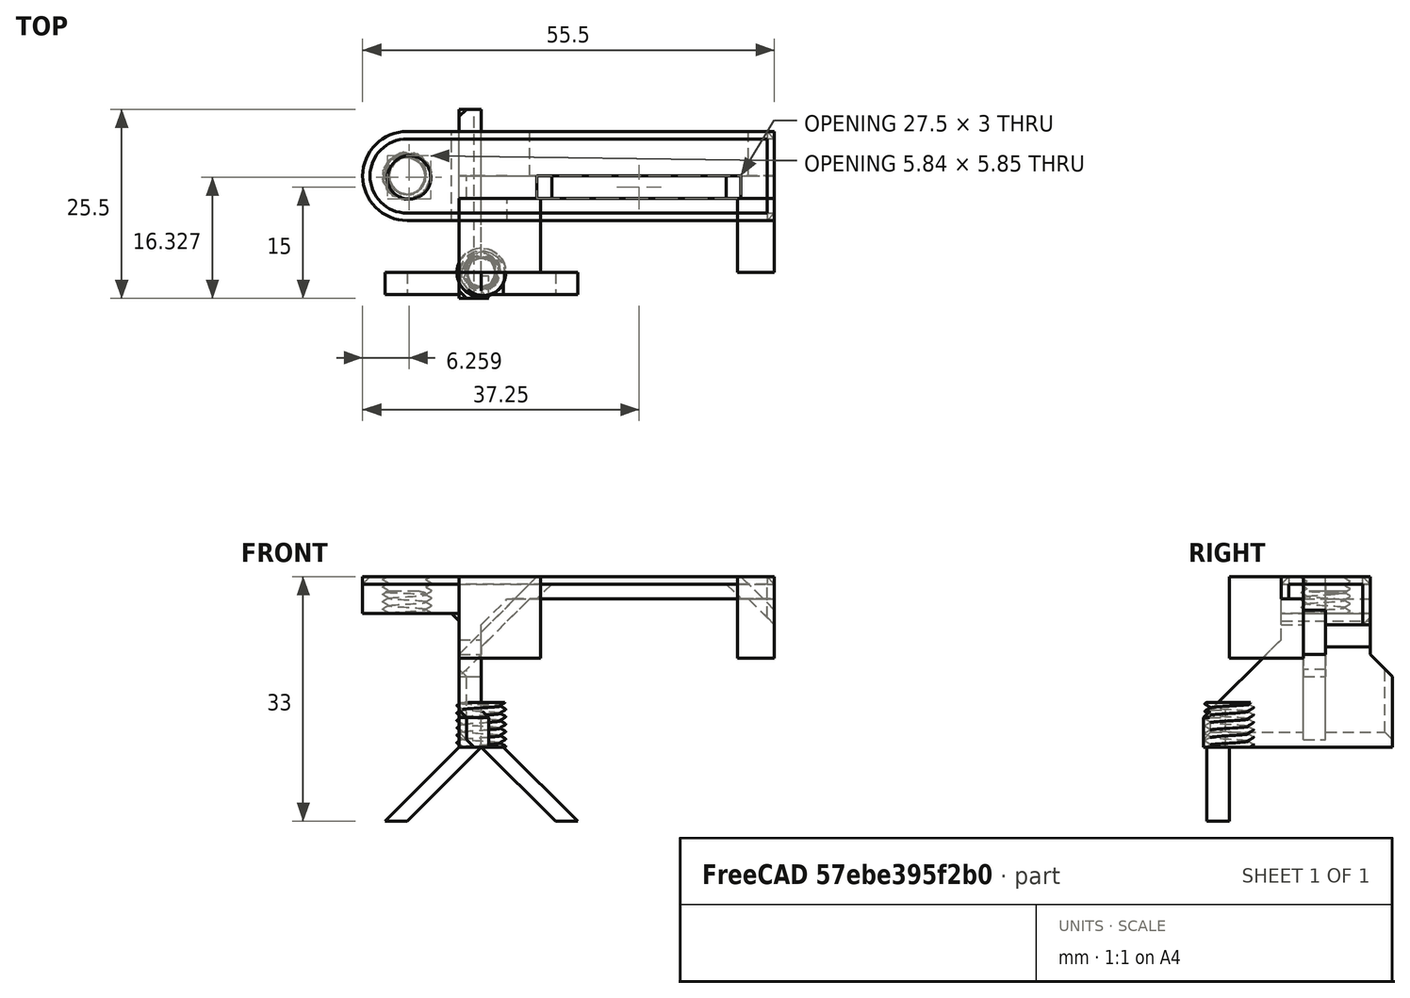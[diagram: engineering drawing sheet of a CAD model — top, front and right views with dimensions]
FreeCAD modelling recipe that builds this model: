
FCSTD DOCUMENT  (FreeCAD 0.18R14555 (Git shallow))
Label: rev-bowden-on-X-fix
License: All rights reserved
LicenseURL: http://en.wikipedia.org/wiki/All_rights_reserved
objects: Part::Box×13, Part::Cut×11, Part::Chamfer×7, Part::Feature×7, Part::MultiFuse×3, Part::Cylinder×2, Sketcher::SketchObject×1, PartDesign::Pad×1, PartDesign::Body×1, Part::Mirroring×1
note: 48 computed .brp shape members not serialized (recipe doc carries the construction recipe); baked Part::Feature solids carry a one-line shape summary decoded from their .brp

FEATURE [Part::Box] Box  label="Cube"
  AttacherType = Attacher::AttachEngine3D
  Height = 20
  Length = 42.5
  Width = 10
FEATURE [Part::Box] Box001  label="Cube001"
  AttacherType = Attacher::AttachEngine3D
  Height = 23
  Length = 42.5
  Placement = pos=(-3,0,0) rot=(0,0,1;0rad)
  Width = 19
FEATURE [Part::Box] Box002  label="Cube002"
  AttacherType = Attacher::AttachEngine3D
  Height = 11
  Length = 11
  Placement = pos=(-3,0,12) rot=(0,0,1;0rad)
  Width = 10
FEATURE [Part::Box] Box003  label="Cube003"
  AttacherType = Attacher::AttachEngine3D
  Height = 11
  Length = 5
  Placement = pos=(34.5,0,12) rot=(0,0,1;0rad)
  Width = 10
FEATURE [Part::Chamfer] Chamfer
  Base = -> Box
  Edges = 2 edges r=3.5: [Edge2,Edge6]
FEATURE [Part::Cylinder] Cylinder
  Angle = 360
  AttacherType = Attacher::AttachEngine3D
  Height = 5
  Placement = pos=(-10,11,18) rot=(0,0,1;0rad)
  Radius = 6
FEATURE [Sketcher::SketchObject] Sketch
  MapMode = 5
  Placement = pos=(0,0,0) rot=(1,0,0;1.5708rad)
  Support = -> [XZ_Plane]
  sketch-geometry (4):
    g0: LineSegment StartX=0 StartY=0 StartZ=0 EndX=10 EndY=-10 EndZ=0
    g1: LineSegment StartX=0 StartY=0 StartZ=0 EndX=3 EndY=0 EndZ=0
    g2: LineSegment StartX=10 StartY=-10 StartZ=0 EndX=13 EndY=-10 EndZ=0
    g3: LineSegment StartX=13 StartY=-10 StartZ=0 EndX=3 EndY=0 EndZ=0
FEATURE [PartDesign::Pad] Pad
  Length = 3
  Length2 = 100
  Placement = pos=(0,0,0) rot=(1,0,0;1.5708rad)
  Profile = -> Sketch
  Type = 0
FEATURE [PartDesign::Body] Body
  Group = -> [Sketch,Pad]
  Origin = -> Origin
  Tip = -> Pad
FEATURE [Part::Feature] Body001
  Placement = pos=(30.5,13,24.5) rot=(0,0,1;0rad)
  shape: bbox 13 x 3 x 10 mm, 6 faces (baked)
FEATURE [Part::Mirroring] Part__Mirroring  label="Pad (Mirror #1)"
  Base = (0,0,0)
  Normal = (1,0,0)
  Source = -> Pad
FEATURE [Part::Feature] Part__Mirroring001  label="Pad (Mirror #1)001"
  Placement = pos=(11.5,13,24) rot=(0,0,1;0rad)
  shape: bbox 13 x 3 x 10 mm, 6 faces (baked)
FEATURE [Part::Feature] Part__Mirroring002  label="Pad (Mirror #1)002"
  Placement = pos=(4.5,13,17) rot=(0,0,1;0rad)
  shape: bbox 13 x 3 x 10 mm, 6 faces (baked)
FEATURE [Part::Box] Box006  label="Cube006"
  AttacherType = Attacher::AttachEngine3D
  Height = 11
  Length = 1
  Placement = pos=(-3,10,0) rot=(0,0,1;0rad)
  Width = 3
FEATURE [Part::Box] Box007  label="Cube007"
  AttacherType = Attacher::AttachEngine3D
  Height = 1
  Length = 24
  Placement = pos=(9,10,22) rot=(0,0,1;0rad)
  Width = 3
FEATURE [Part::Feature] Part__Feature  label="1"
  shape: bbox 11.55 x 19.8 x 11.8 mm, 29 faces (baked)
FEATURE [Part::Cylinder] Cylinder001
  Angle = 360
  AttacherType = Attacher::AttachEngine3D
  Height = 6
  Radius = 4
FEATURE [Part::Cut] Cut008
  Base = -> Cylinder001
  Tool = -> Part__Feature
FEATURE [Part::Feature] Cut008002  label="Cut010"
  Placement = pos=(-10,11,18) rot=(0,0,1;0rad)
  shape: bbox 6.606 x 6.606 x 6.902 mm, 9 faces (baked)
FEATURE [Part::Feature] Cut008003  label="Cut011"
  Placement = pos=(-10,11,15) rot=(0,0,1;0rad)
  shape: bbox 6.606 x 6.606 x 6.902 mm, 9 faces (baked)
FEATURE [Part::Box] Box011  label="Cube011"
  AttacherType = Attacher::AttachEngine3D
  Height = 20
  Length = 42.5
  Placement = pos=(0,10,0) rot=(0,0,1;0rad)
  Width = 10
FEATURE [Part::Chamfer] Chamfer008
  Base = -> Box011
  Edges = 2 edges r=6.5: [Edge2,Edge6]
FEATURE [Part::Box] Box012  label="Cube012"
  AttacherType = Attacher::AttachEngine3D
  Height = 17
  Length = 44
  Placement = pos=(-3,0,6) rot=(0,0,1;0rad)
  Width = 7
FEATURE [Part::Box] Box004  label="Cube004"
  AttacherType = Attacher::AttachEngine3D
  Height = 5
  Length = 10
  Placement = pos=(-10,5,18) rot=(0,0,1;0rad)
  Width = 12
FEATURE [Part::MultiFuse] Fusion
  Shapes = -> [Cut008003,Cut008002]
FEATURE [Part::MultiFuse] Fusion001
  Shapes = -> [Cylinder,Box004]
FEATURE [Part::Cut] Cut008009
  Base = -> Fusion001
  Placement = pos=(0,2,0) rot=(0,0,1;0rad)
  Tool = -> Fusion
FEATURE [Part::Box] Box014  label="Cube014"
  AttacherType = Attacher::AttachEngine3D
  Height = 5
  Length = 4
  Placement = pos=(-3,-3.5,0) rot=(0,0,1;0rad)
  Width = 3
FEATURE [Part::Box] Box015  label="Cube015"
  AttacherType = Attacher::AttachEngine3D
  Height = 12.5
  Length = 3
  Placement = pos=(-3,16,0) rot=(0,0,1;0rad)
  Width = 4
FEATURE [Part::Chamfer] Chamfer014
  Base = -> Box014
  Edges = 2 edges r=1: [Edge6,Edge10]
FEATURE [Part::Chamfer] Chamfer015
  Base = -> Box015
  Edges = 1 edges r=3: [Edge12]
  Placement = pos=(0,2,0) rot=(0,0,1;0rad)
FEATURE [Part::Box] Box016  label="Cube016"
  AttacherType = Attacher::AttachEngine3D
  Height = 10
  Length = 10
  Placement = pos=(36,0,10) rot=(0,0,1;0rad)
  Width = 10
FEATURE [Part::Cut] Cut
  Base = -> Box001
  Tool = -> Chamfer
FEATURE [Part::Cut] Cut008010
  Base = -> Cut
  Tool = -> Box012
FEATURE [Part::Cut] Cut008011
  Base = -> Cut008010
  Tool = -> Chamfer008
FEATURE [Part::Cut] Cut008012
  Base = -> Cut008011
  Tool = -> Box016
FEATURE [Part::Box] Box013  label="Cube013"
  AttacherType = Attacher::AttachEngine3D
  Height = 14.5
  Length = 3
  Placement = pos=(-3,-3.5,0) rot=(0,0,1;0rad)
  Width = 11.5
FEATURE [Part::Chamfer] Chamfer016
  Base = -> Box013
  Edges = 1 edges r=10.5: [Edge10]
FEATURE [Part::Cut] Cut008013
  Base = -> Cut008012
  Tool = -> Body001
FEATURE [Part::Cut] Cut008014
  Base = -> Cut008013
  Tool = -> Box007
FEATURE [Part::Cut] Cut008015
  Base = -> Cut008014
  Tool = -> Part__Mirroring001
FEATURE [Part::MultiFuse] Fusion002
  Shapes = -> [Cut008009,Cut008015,Chamfer016,Chamfer015,Chamfer014]
FEATURE [Part::Cut] Cut008016
  Base = -> Fusion002
  Tool = -> Part__Mirroring002
FEATURE [Part::Feature] Cut008016001  label="Cut008017"
  shape: bbox 55.5 x 25.5 x 23.43 mm, 44 faces (baked)
FEATURE [Part::Chamfer] Chamfer017
  Base = -> Cut008016001
  Edges = 1 edges r=2: [Edge11]
FEATURE [Part::Cut] Cut008016002
  Base = -> Chamfer017
  Tool = -> Box006
FEATURE [Part::Chamfer] Chamfer018
  Base = -> Cut008016002
  Edges = 9 edges r=1: [Edge7,Edge20,Edge44,Edge67,Edge68,Edge72,Edge73,Edge106,Edge110]
